# Revit family: QF_ELECTROLUXPROFESSIONAL_371241_E7GREDGCFU
name_source: partatom
category: Specialty Equipment
units: mm (PartAtom-declared; Revit-internal decimal feet)

## family parameters
Always vertical = Yes
Cut with Voids When Loaded = No
Enable Cutting in Views = No
Maintain Annotation Orientation = No
Part Type = Normal
Room Calculation Point = No
Round Connector Dimension = Use Diameter
Shared = No
Work Plane-Based = No

## types (1)
- QF_ELECTROLUXPROFESSIONAL_371241_E7GREDGCFU
    Apparent Power = 6000 VA
    Conn Conduit = Yes
    Default Elevation = 0 mm  [stored 0 ft]
    Depth = 730 mm  [stored 2.39501 ft]
    Description = 700XP Half Module Freestanding Electric Char-Grill
    Direct Waste Size = 0"
    FL Amps = 9 A
    HP = 8 HP
    Height = 333 mm
    Manufacturer = ELECTROLUX
    Max Overcurrent Protection = 0 A
    Min Ckt Ampacity = 0 A
    Model = 371064
    Phase = 3
    URL = www.electrolux.com/foodservice
    URL Cutsheet = www.electrolux.com/foodservice
    Volts = 400 V
    Watts = 6000 W
    Weight in Pounds = 88
    Width = 400 mm

note: [stored X ft] marks values corroborated as IEEE doubles in the binary element streams (Revit-internal decimal feet)

## geometry (parser evidence)
native form markers: Blend x8, Sweep x5
no freeform markers — native parametric forms only
